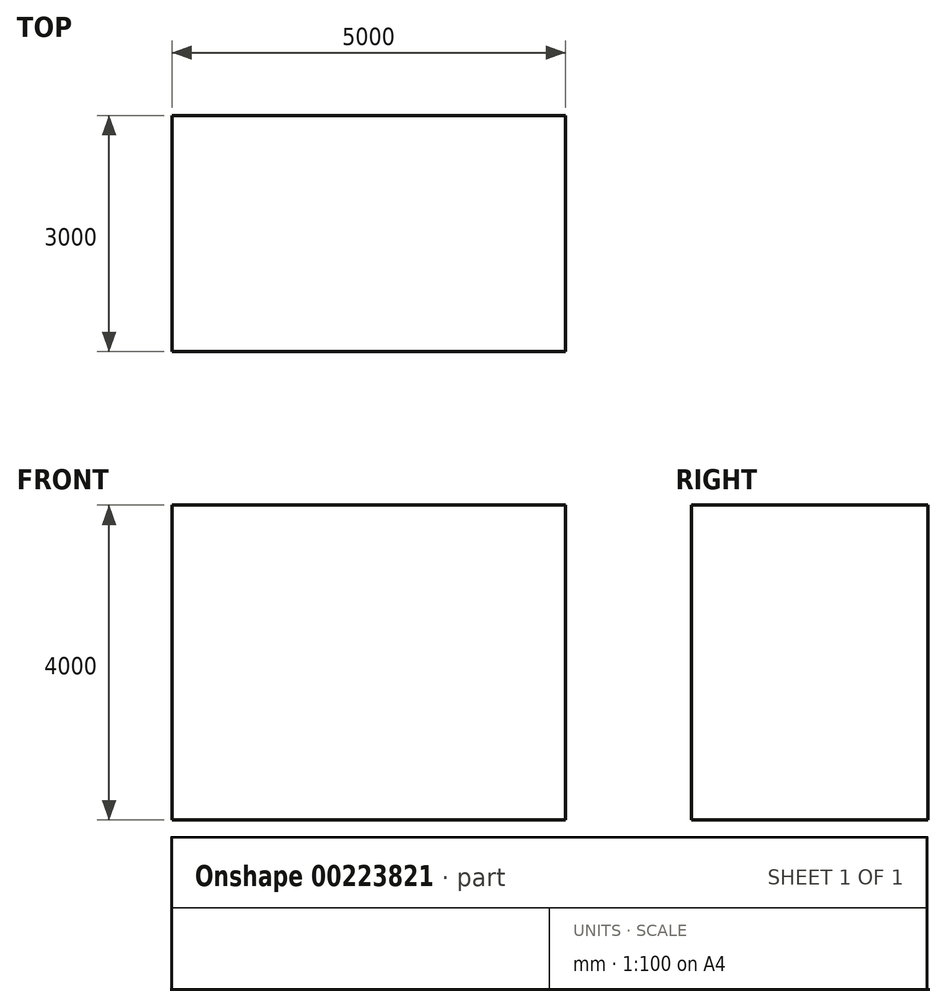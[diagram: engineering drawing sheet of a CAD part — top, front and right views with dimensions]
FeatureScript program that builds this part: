
annotation { "Feature Type Name" : "Feature", "Feature Type Description" : "" }
export const myFeature = defineFeature(function(context is Context, id is Id, definition is map)
    precondition{}
    {
        {
            var Q0;
            Q0=qCreatedBy(makeId("Top.planeOp"),FACE);
            var sketch = newSketch(context, id + "F0", { "sketchPlane" : qUnion([Q0])});
            skLineSegment(sketch, "E0.bottom", {"start": v(0, 0) * mm, "end": v(-5000, 0) * mm});
            skLineSegment(sketch, "E0.top", {"start": v(0, -3000) * mm, "end": v(-5000, -3000) * mm});
            skLineSegment(sketch, "E0.left", {"start": v(0, 0) * mm, "end": v(0, -3000) * mm});
            skLineSegment(sketch, "E0.right", {"start": v(-5000, 0) * mm, "end": v(-5000, -3000) * mm});
            skSolve(sketch);
        }
        {
            var Q0;
            Q0=makeQuery(id+"F0.imprint","IMPRINT",FACE,{"disambiguationData":[TD([[makeQuery(id+"F0.imprint","IMPRINT",EDGE,{"derivedFrom":sQuery(id+"F0.wireOp",EDGE,"E0.bottom")}),1.0]])]});
            extrude(context, id + "F1", {"entities" : qUnion([Q0]), "depth" : 4000 * mm});
        }
    });
